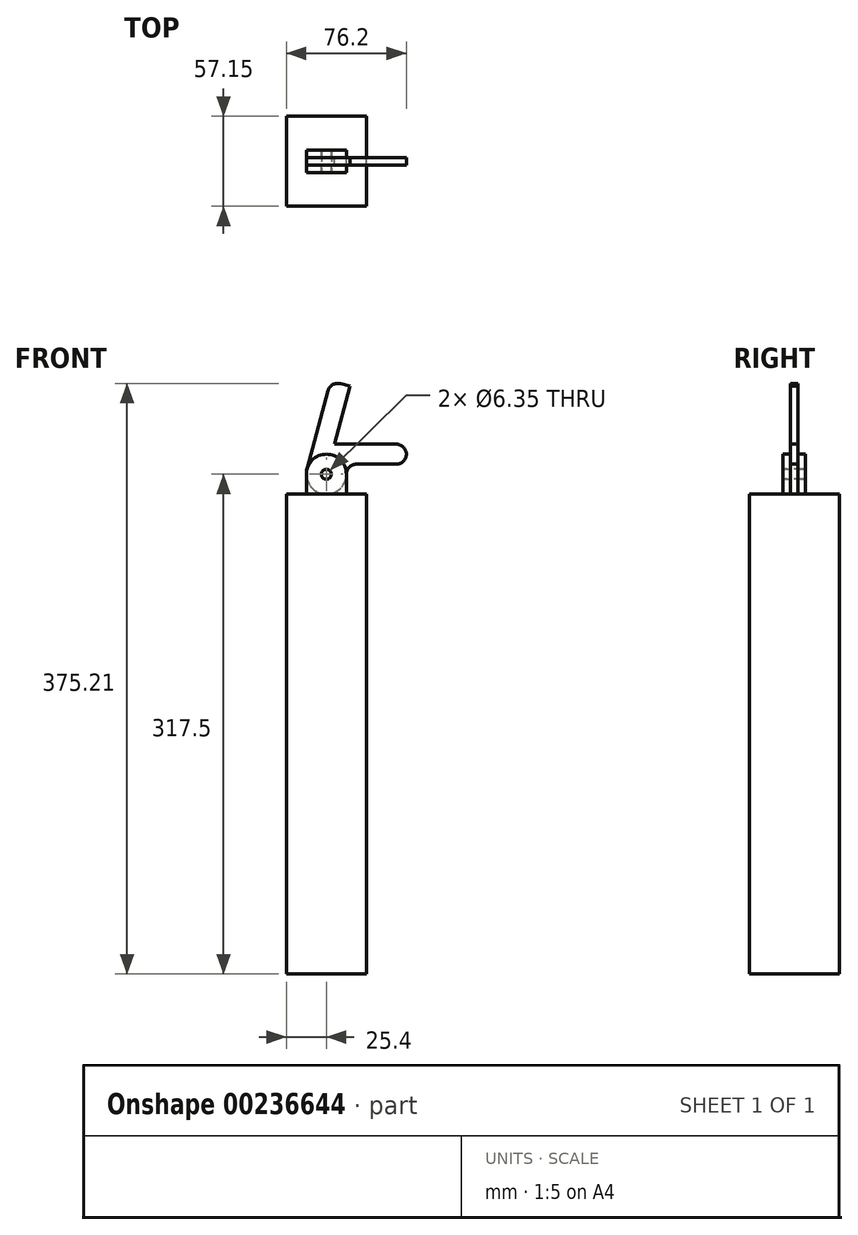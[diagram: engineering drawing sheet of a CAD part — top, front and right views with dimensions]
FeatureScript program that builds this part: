
annotation { "Feature Type Name" : "Feature", "Feature Type Description" : "" }
export const myFeature = defineFeature(function(context is Context, id is Id, definition is map)
    precondition{}
    {
        {
            var Q0;
            Q0=qCreatedBy(makeId("Front.planeOp"),FACE);
            var sketch = newSketch(context, id + "F0", { "sketchPlane" : qUnion([Q0])});
            skCircle(sketch, "E0", {"center": v(0, 0) * mm, "radius": 3.18 * mm});
            skArc(sketch, "E1", {"start": v(12.7, 0) * mm, "mid": v(0, 12.7) * mm, "end": v(-12.7, 0) * mm});
            skLineSegment(sketch, "E2", {"start": v(-12.7, 0) * mm, "end": v(-12.7, -12.7) * mm});
            skLineSegment(sketch, "E3", {"start": v(12.7, 0) * mm, "end": v(12.7, -12.7) * mm});
            skLineSegment(sketch, "E4", {"start": v(0, -12.7) * mm, "end": v(12.7, -12.7) * mm});
            skLineSegment(sketch, "E5", {"start": v(0, -12.7) * mm, "end": v(-12.7, -12.7) * mm});
            skSolve(sketch);
        }
        {
            var Q0;
            Q0=makeQuery(id+"F0.imprint","IMPRINT",FACE,{"disambiguationData":[TD([[makeQuery(id+"F0.imprint","IMPRINT",EDGE,{"derivedFrom":sQuery(id+"F0.wireOp",EDGE,"E0")}),-1.0]])]});
            extrude(context, id + "F1", {"entities" : qUnion([Q0]), "depth" : 4.76 * mm});
        }
        {
            var Q0;
            Q0=makeQuery(id+"F1.opExtrude","SWEPT_BODY",BODY,{"disambiguationData":[OSD([sQuery(id+"F0.wireOp",EDGE,"E0"),sQuery(id+"F0.wireOp",EDGE,"E1"),sQuery(id+"F0.wireOp",EDGE,"E2"),sQuery(id+"F0.wireOp",EDGE,"E3"),sQuery(id+"F0.wireOp",EDGE,"E4"),sQuery(id+"F0.wireOp",EDGE,"E5")])]});
            transform(context, id + "F2", {"entities" : qUnion([Q0]), "transformType" : TransformType.TRANSLATION_3D, "dx" : 0 * mm, "dy" : 9.52 * mm, "dz" : 0 * mm, "makeCopy" : true});
        }
        {
            var Q0;
            Q0=makeQuery(id+"F0.imprint","IMPRINT",FACE,{"disambiguationData":[TD([[makeQuery(id+"F0.imprint","IMPRINT",EDGE,{"derivedFrom":sQuery(id+"F0.wireOp",EDGE,"E0")}),1.0]])]});
            extrude(context, id + "F3", {"entities" : qUnion([Q0]), "oppositeDirection" : true, "depth" : 9.52 * mm, "hasSecondDirection" : true, "secondDirectionOppositeDirection" : false, "secondDirectionDepth" : 4.76 * mm});
        }
        {
            var Q0;
            Q0=makeQuery(id+"F2.opPattern","COPY",FACE,{"derivedFrom":makeQuery(id+"F1.opExtrude","CAP_FACE",FACE,{"disambiguationData":[OSD([sQuery(id+"F0.wireOp",EDGE,"E0"),sQuery(id+"F0.wireOp",EDGE,"E1"),sQuery(id+"F0.wireOp",EDGE,"E2"),sQuery(id+"F0.wireOp",EDGE,"E3"),sQuery(id+"F0.wireOp",EDGE,"E4"),sQuery(id+"F0.wireOp",EDGE,"E5")])],"isStart":false}),"instanceName":"1"});
            cPlane(context, id + "F4", {"entities" : qUnion([Q0]), "cplaneType" : CPlaneType.OFFSET, "offset" : 2.38 * mm, "width" : 152.4 * mm, "height" : 152.4 * mm});
        }
        {
            var Q0;
            Q0=qCreatedBy(id+"F4.planeOp",FACE);
            var sketch = newSketch(context, id + "F5", { "sketchPlane" : qUnion([Q0])});
            skLineSegment(sketch, "E6", {"start": v(50.8, 12.7) * mm, "end": v(50.8, 12.7) * mm});
            skLineSegment(sketch, "E7", {"start": v(44.45, 19.05) * mm, "end": v(5.1, 19.05) * mm});
            skPoint(sketch, "E8.visualSharp", {"position": v(50.8, 19.05) * mm});
            skArc(sketch, "E8.filletArc", {"start": v(50.8, 12.7) * mm, "mid": v(48.94, 17.2) * mm, "end": v(44.45, 19.05) * mm});
            skPoint(sketch, "E9.visualSharp", {"position": v(50.8, 6.35) * mm});
            skPoint(sketch, "E10.visualSharp", {"position": v(12.7, 0) * mm});
            skLineSegment(sketch, "E11", {"start": v(12.7, 0) * mm, "end": v(12.7, 0) * mm});
            skLineSegment(sketch, "E12", {"start": v(19.05, 6.35) * mm, "end": v(44.45, 6.35) * mm});
            skPoint(sketch, "E13.visualSharp", {"position": v(12.7, 6.35) * mm});
            skArc(sketch, "E13.filletArc", {"start": v(19.05, 6.35) * mm, "mid": v(14.56, 4.5) * mm, "end": v(12.7, 0) * mm});
            skArc(sketch, "E14.filletArc", {"start": v(44.45, 6.35) * mm, "mid": v(48.94, 8.2) * mm, "end": v(50.8, 12.7) * mm});
            skLineSegment(sketch, "E15", {"start": v(-12.27, 3.29) * mm, "end": v(1.05, 53) * mm});
            skLineSegment(sketch, "E16", {"start": v(8.83, 57.5) * mm, "end": v(14.97, 55.85) * mm});
            skLineSegment(sketch, "E17", {"start": v(14.97, 55.85) * mm, "end": v(5.1, 19.05) * mm});
            skArc(sketch, "E18", {"start": v(-12.27, 3.29) * mm, "mid": v(-1.66, -12.6) * mm, "end": v(12.7, 0) * mm});
            skPoint(sketch, "E19.visualSharp", {"position": v(2.7, 59.14) * mm});
            skArc(sketch, "E19.filletArc", {"start": v(8.83, 57.5) * mm, "mid": v(4.01, 56.86) * mm, "end": v(1.05, 53) * mm});
            skSolve(sketch);
        }
        {
            var Q0;
            Q0=makeQuery(id+"F5.imprint","IMPRINT",FACE,{"disambiguationData":[TD([[makeQuery(id+"F5.imprint","IMPRINT",EDGE,{"derivedFrom":sQuery(id+"F5.wireOp",EDGE,"ZBOrRvWA-Zsny-QJQH-aAW1-NDks2fAVxMMG")}),1.0]])]});
            var Q1;
            {var subQ1=sQuery(id+"F5.wireOp",EDGE,"qktoMMUk-6ylO-f5TV-pOuF-03LsLpky7e9K");Q1=makeQuery(id+"F5.imprint","IMPRINT",FACE,{"disambiguationData":[TD([[makeQuery(id+"F5.imprint","IMPRINT",EDGE,{"derivedFrom":subQ1}),1.0]])]});}
            var Q2;
            Q2=makeQuery(id+"F5.imprint","IMPRINT",FACE,{"disambiguationData":[TD([[makeQuery(id+"F5.imprint","IMPRINT",EDGE,{"derivedFrom":sQuery(id+"F5.wireOp",EDGE,"E7")}),1.0]])]});
            extrude(context, id + "F6", {"entities" : qUnion([Q0, Q1, Q2]), "depth" : 4.76 * mm, "symmetric" : true});
        }
        {
            var Q0;
            Q0=makeQuery(id+"F1.opExtrude","SWEPT_FACE",FACE,{"disambiguationData":[OSD([sQuery(id+"F0.wireOp",EDGE,"E4"),sQuery(id+"F0.wireOp",EDGE,"E5")])]});
            var sketch = newSketch(context, id + "F7", { "sketchPlane" : qUnion([Q0])});
            skLineSegment(sketch, "E20.bottom", {"start": v(-25.4, 26.2) * mm, "end": v(25.4, 26.2) * mm});
            skLineSegment(sketch, "E20.top", {"start": v(-25.4, -30.96) * mm, "end": v(25.4, -30.96) * mm});
            skLineSegment(sketch, "E20.left", {"start": v(-25.4, 26.2) * mm, "end": v(-25.4, -30.96) * mm});
            skLineSegment(sketch, "E20.right", {"start": v(25.4, 26.2) * mm, "end": v(25.4, -30.96) * mm});
            skSolve(sketch);
        }
        {
            var Q0;
            Q0=makeQuery(id+"F7.imprint","IMPRINT",FACE,{"disambiguationData":[TD([[makeQuery(id+"F7.imprint","IMPRINT",EDGE,{"derivedFrom":sQuery(id+"F7.wireOp",EDGE,"E20.bottom")}),-1.0]])]});
            var Q1;
            {var subQ0=sQuery(id+"F0.wireOp",EDGE,"E5");Q1=makeQuery(id+"F7.imprint","IMPRINT",FACE,{"disambiguationData":[TD([[makeQuery(id+"F7.imprint","IMPRINT",EDGE,{"derivedFrom":makeQuery(id+"F1.opExtrude","SWEPT_EDGE",EDGE,{"disambiguationData":[OSD([sQuery(id+"F0.wireOp",EDGE,"E2"),subQ0])]})}),1.0]])]});}
            extrude(context, id + "F8", {"entities" : qUnion([Q0, Q1]), "depth" : 304.8 * mm});
        }
    });
